# Revit family: Toilet-Floor_Mount-KOHLER-San_Raphael-K-3722
name_source: partatom
category: Plumbing Fixtures
revit_build: Autodesk Revit 2015 (Build: 20140606_1530(x64)
units: mm (PartAtom-declared; Revit-internal decimal feet)

## types (1)
- 0-White
    ADA Compliant = No
    Assembly Code = D2010100
    CW Connection = Yes
    Cold Water Inlet = Cold Water Inlet
    Date Modified = 07/30/2018
    Default Elevation = 0"
    Description = Skirted one-piece elongated 1.28 gpf toilet with left-hand trip lever
    Finish = Kohler-Vitreous_China-0-White
    Flow Rate = 0 GPM
    Flush Rate = 1.28 GPF
    HW Connection = No
    Height = 24"
    Hot Water Inlet = Hot Water Inlet
    Length = 29"
    Manufacturer = KOHLER Co.
    MasterFormat 1995 = 15410
    MasterFormat 2004 = 22.41.13
    Material = Vitreous china
    Model = K-3722-0
    Pressure = 0.00 psi
    Product Documentation Link = http://www.us.kohler.com
    Product Name = San Raphael
    Product Page URL = http://www.us.kohler.com
    Rough-In = 12"
    Seat Included = Yes
    URL = https://www.us.kohler.com
    Vent Connection = No
    Waste Connection = Yes
    Waste Water Outlet = Waste Water Outlet
    Width = 20 1/2"

## geometry (parser evidence)
native form markers: Sweep x5
no freeform markers — native parametric forms only
